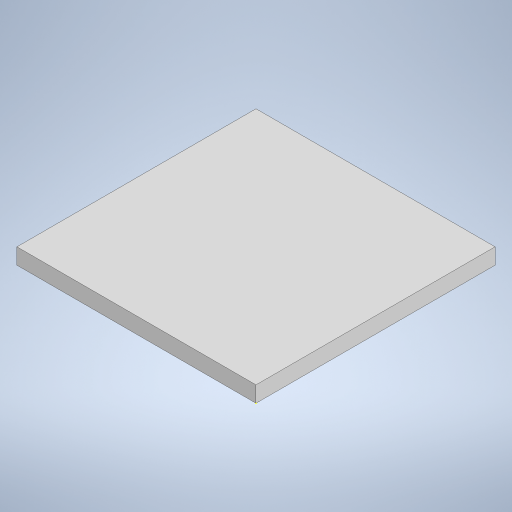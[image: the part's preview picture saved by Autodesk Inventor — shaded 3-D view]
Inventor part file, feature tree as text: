
AUTODESK INVENTOR PART (.ipt)
format: ipt  version: 2023 (Build 270158000, 158)  size: 196,096 bytes
history: native  units: mm
features: sketch x2, extrude x1
ambient origin geometry x8: Origin, YZ Plane, XZ Plane, XY Plane, X Axis, Y Axis, Z Axis, Center Point
bodies: Solid1 (feature_tree)
feature tree (3):
  sketch  "Sketch1"  dims[d0=15.0114mm d1=1.0mm d2=0.0mm]
  extrude  "Extrusion1"  Depth=1.0mm TaperAngle=0.0deg
  sketch  "Sketch2"
